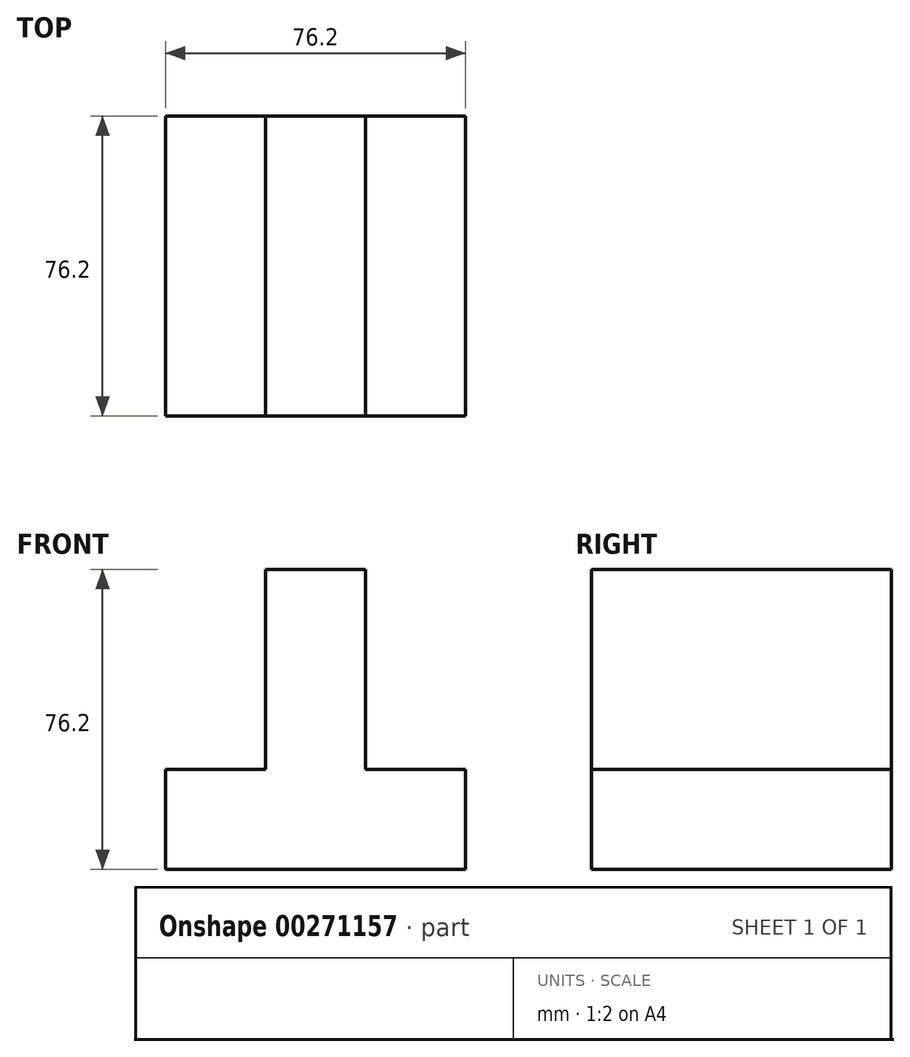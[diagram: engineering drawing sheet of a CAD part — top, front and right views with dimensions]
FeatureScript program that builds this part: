
annotation { "Feature Type Name" : "Feature", "Feature Type Description" : "" }
export const myFeature = defineFeature(function(context is Context, id is Id, definition is map)
    precondition{}
    {
        {
            var Q0;
            Q0=qCreatedBy(makeId("Front.planeOp"),FACE);
            var sketch = newSketch(context, id + "F0", { "sketchPlane" : qUnion([Q0])});
            skLineSegment(sketch, "E0", {"start": v(0, 0) * mm, "end": v(-76.2, 0) * mm});
            skLineSegment(sketch, "E1", {"start": v(-76.2, 0) * mm, "end": v(-76.2, 25.4) * mm});
            skLineSegment(sketch, "E2", {"start": v(-76.2, 25.4) * mm, "end": v(-50.8, 25.4) * mm});
            skLineSegment(sketch, "E3", {"start": v(-50.8, 25.4) * mm, "end": v(-50.8, 76.2) * mm});
            skLineSegment(sketch, "E4", {"start": v(-50.8, 76.2) * mm, "end": v(-25.4, 76.2) * mm});
            skLineSegment(sketch, "E5", {"start": v(-25.4, 76.2) * mm, "end": v(-25.4, 25.4) * mm});
            skLineSegment(sketch, "E6", {"start": v(-25.4, 25.4) * mm, "end": v(0, 25.4) * mm});
            skLineSegment(sketch, "E7", {"start": v(0, 25.4) * mm, "end": v(0, 0) * mm});
            skSolve(sketch);
        }
        {
            var Q0;
            Q0=makeQuery(id+"F0.imprint","IMPRINT",FACE,{"disambiguationData":[TD([[makeQuery(id+"F0.imprint","IMPRINT",EDGE,{"derivedFrom":sQuery(id+"F0.wireOp",EDGE,"E0")}),-1.0]])]});
            extrude(context, id + "F1", {"entities" : qUnion([Q0]), "depth" : 76.2 * mm});
        }
    });
